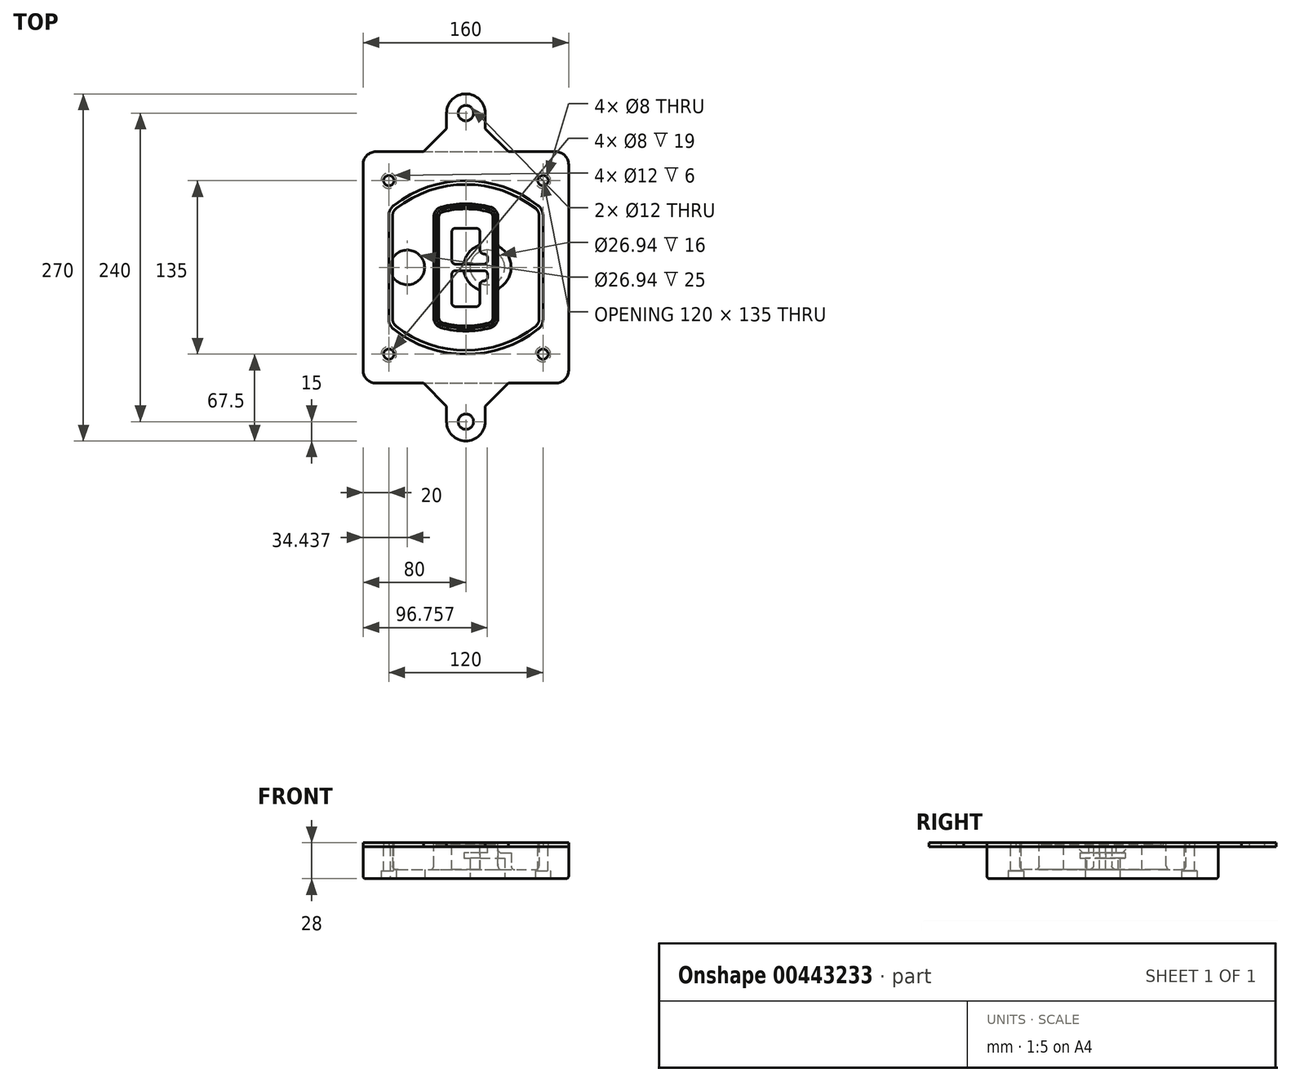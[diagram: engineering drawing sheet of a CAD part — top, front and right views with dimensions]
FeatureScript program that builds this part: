
annotation { "Feature Type Name" : "Feature", "Feature Type Description" : "" }
export const myFeature = defineFeature(function(context is Context, id is Id, definition is map)
    precondition{}
    {
        {
            var Q0;
            Q0=qCreatedBy(makeId("Top.planeOp"),FACE);
            var sketch = newSketch(context, id + "F0", { "sketchPlane" : qUnion([Q0])});
            skPoint(sketch, "E0.rect.middle", {"position": v(0, 0) * mm});
            skLineSegment(sketch, "E1.bottom", {"start": v(-70, -90) * mm, "end": v(70, -90) * mm});
            skLineSegment(sketch, "E1.top", {"start": v(-70, 90) * mm, "end": v(70, 90) * mm});
            skLineSegment(sketch, "E1.left", {"start": v(-80, -80) * mm, "end": v(-80, 80) * mm});
            skLineSegment(sketch, "E1.right", {"start": v(80, -80) * mm, "end": v(80, 80) * mm});
            skLineSegment(sketch, "E2", {"start": v(-80, 90) * mm, "end": v(80, -90) * mm, "construction": true});
            skLineSegment(sketch, "E3", {"start": v(80, 90) * mm, "end": v(-80, -90) * mm, "construction": true});
            skCircle(sketch, "E4", {"center": v(-60, 67.5) * mm, "radius": 4 * mm});
            skCircle(sketch, "E5", {"center": v(60, 67.5) * mm, "radius": 4 * mm});
            skCircle(sketch, "E6", {"center": v(60, -67.5) * mm, "radius": 4 * mm});
            skCircle(sketch, "E7", {"center": v(-60, -67.5) * mm, "radius": 4 * mm});
            skLineSegment(sketch, "E8", {"start": v(-60, 67.5) * mm, "end": v(60, 67.5) * mm, "construction": true});
            skLineSegment(sketch, "E9", {"start": v(60, 67.5) * mm, "end": v(60, -67.5) * mm, "construction": true});
            skLineSegment(sketch, "E10", {"start": v(60, -67.5) * mm, "end": v(-60, -67.5) * mm, "construction": true});
            skLineSegment(sketch, "E11", {"start": v(-60, -67.5) * mm, "end": v(-60, 67.5) * mm, "construction": true});
            skLineSegment(sketch, "E12", {"start": v(-60, 40.3) * mm, "end": v(-60, -40.3) * mm});
            skLineSegment(sketch, "E13", {"start": v(60, 40.3) * mm, "end": v(60, -40.3) * mm});
            skArc(sketch, "E14", {"start": v(56.15, 48.18) * mm, "mid": v(0, 67.5) * mm, "end": v(-56.15, 48.18) * mm});
            skArc(sketch, "E15", {"start": v(-56.15, -48.18) * mm, "mid": v(0, -67.5) * mm, "end": v(56.15, -48.18) * mm});
            skLineSegment(sketch, "E16", {"start": v(-60, 0) * mm, "end": v(60, 0) * mm, "construction": true});
            skPoint(sketch, "E17.visualSharp", {"position": v(-60, -45) * mm});
            skArc(sketch, "E17.filletArc", {"start": v(-60, -40.3) * mm, "mid": v(-58.99, -44.68) * mm, "end": v(-56.15, -48.18) * mm});
            skPoint(sketch, "E18.visualSharp", {"position": v(-60, 45) * mm});
            skArc(sketch, "E18.filletArc", {"start": v(-56.15, 48.18) * mm, "mid": v(-58.99, 44.68) * mm, "end": v(-60, 40.3) * mm});
            skPoint(sketch, "E19.visualSharp", {"position": v(60, 45) * mm});
            skArc(sketch, "E19.filletArc", {"start": v(60, 40.3) * mm, "mid": v(58.99, 44.68) * mm, "end": v(56.15, 48.18) * mm});
            skPoint(sketch, "E20.visualSharp", {"position": v(60, -45) * mm});
            skArc(sketch, "E20.filletArc", {"start": v(56.15, -48.18) * mm, "mid": v(58.99, -44.68) * mm, "end": v(60, -40.3) * mm});
            skPoint(sketch, "E21.visualSharp", {"position": v(-80, 90) * mm});
            skArc(sketch, "E21.filletArc", {"start": v(-70, 90) * mm, "mid": v(-77.07, 87.07) * mm, "end": v(-80, 80) * mm});
            skPoint(sketch, "E22.visualSharp", {"position": v(80, 90) * mm});
            skArc(sketch, "E22.filletArc", {"start": v(80, 80) * mm, "mid": v(77.07, 87.07) * mm, "end": v(70, 90) * mm});
            skPoint(sketch, "E23.visualSharp", {"position": v(80, -90) * mm});
            skArc(sketch, "E23.filletArc", {"start": v(70, -90) * mm, "mid": v(77.07, -87.07) * mm, "end": v(80, -80) * mm});
            skPoint(sketch, "E24.visualSharp", {"position": v(-80, -90) * mm});
            skArc(sketch, "E24.filletArc", {"start": v(-80, -80) * mm, "mid": v(-77.07, -87.07) * mm, "end": v(-70, -90) * mm});
            skArc(sketch, "E25.0", {"start": v(57, 40.3) * mm, "mid": v(56.3, 43.36) * mm, "end": v(54.3, 45.81) * mm});
            skLineSegment(sketch, "E25.1", {"start": v(57, 40.3) * mm, "end": v(57, -40.3) * mm});
            skArc(sketch, "E25.2", {"start": v(54.3, -45.81) * mm, "mid": v(56.3, -43.36) * mm, "end": v(57, -40.3) * mm});
            skArc(sketch, "E25.3", {"start": v(-54.3, -45.81) * mm, "mid": v(0, -64.5) * mm, "end": v(54.3, -45.81) * mm});
            skArc(sketch, "E25.4", {"start": v(-57, -40.3) * mm, "mid": v(-56.3, -43.36) * mm, "end": v(-54.3, -45.81) * mm});
            skArc(sketch, "E25.5", {"start": v(54.3, 45.81) * mm, "mid": v(0, 64.5) * mm, "end": v(-54.3, 45.81) * mm});
            skLineSegment(sketch, "E25.6", {"start": v(-57, 40.3) * mm, "end": v(-57, -40.3) * mm});
            skArc(sketch, "E25.7", {"start": v(-54.3, 45.81) * mm, "mid": v(-56.3, 43.36) * mm, "end": v(-57, 40.3) * mm});
            skArc(sketch, "E26.0", {"start": v(-58.62, 51.33) * mm, "mid": v(-62.58, 46.43) * mm, "end": v(-64, 40.3) * mm});
            skArc(sketch, "E26.1", {"start": v(58.62, 51.33) * mm, "mid": v(0, 71.5) * mm, "end": v(-58.62, 51.33) * mm});
            skArc(sketch, "E26.2", {"start": v(64, 40.3) * mm, "mid": v(62.58, 46.43) * mm, "end": v(58.62, 51.33) * mm});
            skLineSegment(sketch, "E26.3", {"start": v(64, 40.3) * mm, "end": v(64, -40.3) * mm});
            skArc(sketch, "E26.4", {"start": v(58.62, -51.33) * mm, "mid": v(62.58, -46.43) * mm, "end": v(64, -40.3) * mm});
            skLineSegment(sketch, "E26.5", {"start": v(-64, 40.3) * mm, "end": v(-64, -40.3) * mm});
            skArc(sketch, "E26.6", {"start": v(-58.62, -51.33) * mm, "mid": v(0, -71.5) * mm, "end": v(58.62, -51.33) * mm});
            skArc(sketch, "E26.7", {"start": v(-64, -40.3) * mm, "mid": v(-62.58, -46.43) * mm, "end": v(-58.62, -51.33) * mm});
            skSolve(sketch);
        }
        {
            var Q0;
            Q0=makeQuery(id+"F0.imprint","IMPRINT",FACE,{"disambiguationData":[TD([[makeQuery(id+"F0.imprint","IMPRINT",EDGE,{"derivedFrom":sQuery(id+"F0.wireOp",EDGE,"E1.bottom")}),1.0]])]});
            var Q1;
            Q1=makeQuery(id+"F0.imprint","IMPRINT",FACE,{"disambiguationData":[TD([[makeQuery(id+"F0.imprint","IMPRINT",EDGE,{"derivedFrom":sQuery(id+"F0.wireOp",EDGE,"E12")}),1.0]])]});
            var Q2;
            Q2=makeQuery(id+"F0.imprint","IMPRINT",FACE,{"disambiguationData":[TD([[makeQuery(id+"F0.imprint","IMPRINT",EDGE,{"derivedFrom":sQuery(id+"F0.wireOp",EDGE,"E25.0")}),1.0]])]});
            var Q3;
            Q3=makeQuery(id+"F0.imprint","IMPRINT",FACE,{"disambiguationData":[TD([[makeQuery(id+"F0.imprint","IMPRINT",EDGE,{"derivedFrom":sQuery(id+"F0.wireOp",EDGE,"E12")}),-1.0]])]});
            extrude(context, id + "F1", {"entities" : qUnion([Q0, Q1, Q2, Q3]), "oppositeDirection" : true, "depth" : 25 * mm});
        }
        {
            var Q0;
            Q0=makeQuery(id+"F0.imprint","IMPRINT",FACE,{"disambiguationData":[TD([[makeQuery(id+"F0.imprint","IMPRINT",EDGE,{"derivedFrom":sQuery(id+"F0.wireOp",EDGE,"E12")}),1.0]])]});
            extrude(context, id + "F2", {"entities" : qUnion([Q0]), "operationType" : NewBodyOperationType.ADD, "depth" : 3 * mm});
        }
        {
            var Q0;
            Q0=makeQuery(id+"F0.imprint","IMPRINT",FACE,{"disambiguationData":[TD([[makeQuery(id+"F0.imprint","IMPRINT",EDGE,{"derivedFrom":sQuery(id+"F0.wireOp",EDGE,"E25.0")}),1.0]])]});
            extrude(context, id + "F3", {"entities" : qUnion([Q0]), "operationType" : NewBodyOperationType.REMOVE, "oppositeDirection" : true, "depth" : 18 * mm});
        }
        {
            var Q0;
            Q0=makeQuery(id+"F2.opExtrude","CAP_FACE",FACE,{"disambiguationData":[OSD([sQuery(id+"F0.wireOp",EDGE,"E12"),sQuery(id+"F0.wireOp",EDGE,"E13"),sQuery(id+"F0.wireOp",EDGE,"E14"),sQuery(id+"F0.wireOp",EDGE,"E15"),sQuery(id+"F0.wireOp",EDGE,"E17.filletArc"),sQuery(id+"F0.wireOp",EDGE,"E18.filletArc"),sQuery(id+"F0.wireOp",EDGE,"E19.filletArc"),sQuery(id+"F0.wireOp",EDGE,"E20.filletArc"),sQuery(id+"F0.wireOp",EDGE,"E25.0"),sQuery(id+"F0.wireOp",EDGE,"E25.1"),sQuery(id+"F0.wireOp",EDGE,"E25.2"),sQuery(id+"F0.wireOp",EDGE,"E25.3"),sQuery(id+"F0.wireOp",EDGE,"E25.4"),sQuery(id+"F0.wireOp",EDGE,"E25.5"),sQuery(id+"F0.wireOp",EDGE,"E25.6"),sQuery(id+"F0.wireOp",EDGE,"E25.7")])],"isStart":false});
            var sketch = newSketch(context, id + "F4", { "sketchPlane" : qUnion([Q0])});
            skArc(sketch, "E27.0", {"start": v(-19.08, -46.97) * mm, "mid": v(0, -49.5) * mm, "end": v(19.08, -46.97) * mm});
            skArc(sketch, "E28.0", {"start": v(19.08, 46.97) * mm, "mid": v(0, 49.5) * mm, "end": v(-19.08, 46.97) * mm});
            skLineSegment(sketch, "E29", {"start": v(-25, 39.25) * mm, "end": v(-25, -39.25) * mm});
            skLineSegment(sketch, "E30", {"start": v(25, 39.25) * mm, "end": v(25, -39.25) * mm});
            skLineSegment(sketch, "E31", {"start": v(-25, 45.1) * mm, "end": v(25, 45.1) * mm, "construction": true});
            skLineSegment(sketch, "E32", {"start": v(-25, -45.1) * mm, "end": v(25, -45.1) * mm, "construction": true});
            skPoint(sketch, "E33.visualSharp", {"position": v(-25, 45.1) * mm});
            skArc(sketch, "E33.filletArc", {"start": v(-19.08, 46.97) * mm, "mid": v(-23.35, 44.11) * mm, "end": v(-25, 39.25) * mm});
            skPoint(sketch, "E34.visualSharp", {"position": v(25, 45.1) * mm});
            skArc(sketch, "E34.filletArc", {"start": v(25, 39.25) * mm, "mid": v(23.35, 44.11) * mm, "end": v(19.08, 46.97) * mm});
            skPoint(sketch, "E35.visualSharp", {"position": v(25, -45.1) * mm});
            skArc(sketch, "E35.filletArc", {"start": v(19.08, -46.97) * mm, "mid": v(23.35, -44.11) * mm, "end": v(25, -39.25) * mm});
            skPoint(sketch, "E36.visualSharp", {"position": v(-25, -45.1) * mm});
            skArc(sketch, "E36.filletArc", {"start": v(-25, -39.25) * mm, "mid": v(-23.35, -44.11) * mm, "end": v(-19.08, -46.97) * mm});
            skArc(sketch, "E37.0", {"start": v(54.3, 45.81) * mm, "mid": v(0, 64.5) * mm, "end": v(-54.3, 45.81) * mm});
            skArc(sketch, "E37.1", {"start": v(-54.3, 45.81) * mm, "mid": v(-56.3, 43.36) * mm, "end": v(-57, 40.3) * mm});
            skLineSegment(sketch, "E37.2", {"start": v(-57, 40.3) * mm, "end": v(-57, -40.3) * mm});
            skArc(sketch, "E37.3", {"start": v(-57, -40.3) * mm, "mid": v(-56.3, -43.36) * mm, "end": v(-54.3, -45.81) * mm});
            skArc(sketch, "E37.4", {"start": v(-54.3, -45.81) * mm, "mid": v(0, -64.5) * mm, "end": v(54.3, -45.81) * mm});
            skArc(sketch, "E37.5", {"start": v(54.3, -45.81) * mm, "mid": v(56.3, -43.36) * mm, "end": v(57, -40.3) * mm});
            skLineSegment(sketch, "E37.6", {"start": v(57, 40.3) * mm, "end": v(57, -40.3) * mm});
            skArc(sketch, "E37.7", {"start": v(57, 40.3) * mm, "mid": v(56.3, 43.36) * mm, "end": v(54.3, 45.81) * mm});
            skLineSegment(sketch, "E38.0", {"start": v(23, 39.25) * mm, "end": v(23, -39.25) * mm});
            skArc(sketch, "E38.1", {"start": v(18.56, -45.04) * mm, "mid": v(21.76, -42.9) * mm, "end": v(23, -39.25) * mm});
            skArc(sketch, "E38.2", {"start": v(-18.56, -45.04) * mm, "mid": v(0, -47.5) * mm, "end": v(18.56, -45.04) * mm});
            skArc(sketch, "E38.3", {"start": v(-23, -39.25) * mm, "mid": v(-21.76, -42.9) * mm, "end": v(-18.56, -45.04) * mm});
            skLineSegment(sketch, "E38.4", {"start": v(-23, 39.25) * mm, "end": v(-23, -39.25) * mm});
            skArc(sketch, "E38.5", {"start": v(23, 39.25) * mm, "mid": v(21.76, 42.9) * mm, "end": v(18.56, 45.04) * mm});
            skArc(sketch, "E38.6", {"start": v(-18.56, 45.04) * mm, "mid": v(-21.76, 42.9) * mm, "end": v(-23, 39.25) * mm});
            skArc(sketch, "E38.7", {"start": v(18.56, 45.04) * mm, "mid": v(0, 47.5) * mm, "end": v(-18.56, 45.04) * mm});
            skArc(sketch, "E39.0", {"start": v(21, 39.25) * mm, "mid": v(20.18, 41.68) * mm, "end": v(18.04, 43.1) * mm});
            skLineSegment(sketch, "E39.1", {"start": v(21, 39.25) * mm, "end": v(21, -39.25) * mm});
            skArc(sketch, "E39.2", {"start": v(18.04, -43.1) * mm, "mid": v(20.18, -41.68) * mm, "end": v(21, -39.25) * mm});
            skArc(sketch, "E39.3", {"start": v(-18.04, -43.1) * mm, "mid": v(0, -45.5) * mm, "end": v(18.04, -43.1) * mm});
            skArc(sketch, "E39.4", {"start": v(-21, -39.25) * mm, "mid": v(-20.18, -41.68) * mm, "end": v(-18.04, -43.1) * mm});
            skArc(sketch, "E39.5", {"start": v(18.04, 43.1) * mm, "mid": v(0, 45.5) * mm, "end": v(-18.04, 43.1) * mm});
            skLineSegment(sketch, "E39.6", {"start": v(-21, 39.25) * mm, "end": v(-21, -39.25) * mm});
            skArc(sketch, "E39.7", {"start": v(-18.04, 43.1) * mm, "mid": v(-20.18, 41.68) * mm, "end": v(-21, 39.25) * mm});
            skLineSegment(sketch, "E40", {"start": v(-25, 0) * mm, "end": v(25, 0) * mm, "construction": true});
            skLineSegment(sketch, "E41", {"start": v(-11, 5.5) * mm, "end": v(-11, 27.5) * mm});
            skLineSegment(sketch, "E42", {"start": v(-8, 30.5) * mm, "end": v(8, 30.5) * mm});
            skLineSegment(sketch, "E43", {"start": v(11, 27.5) * mm, "end": v(11, 13.5) * mm});
            skLineSegment(sketch, "E44", {"start": v(14, 10.5) * mm, "end": v(14, 10.5) * mm});
            skLineSegment(sketch, "E45", {"start": v(17, 7.5) * mm, "end": v(17, 5.5) * mm});
            skLineSegment(sketch, "E46", {"start": v(14, 2.5) * mm, "end": v(-8, 2.5) * mm});
            skPoint(sketch, "E47.visualSharp", {"position": v(-11, 30.5) * mm});
            skArc(sketch, "E47.filletArc", {"start": v(-8, 30.5) * mm, "mid": v(-10.12, 29.62) * mm, "end": v(-11, 27.5) * mm});
            skPoint(sketch, "E48.visualSharp", {"position": v(11, 30.5) * mm});
            skArc(sketch, "E48.filletArc", {"start": v(11, 27.5) * mm, "mid": v(10.12, 29.62) * mm, "end": v(8, 30.5) * mm});
            skPoint(sketch, "E49.visualSharp", {"position": v(11, 10.5) * mm});
            skArc(sketch, "E49.filletArc", {"start": v(11, 13.5) * mm, "mid": v(11.88, 11.38) * mm, "end": v(14, 10.5) * mm});
            skPoint(sketch, "E50.visualSharp", {"position": v(17, 10.5) * mm});
            skArc(sketch, "E50.filletArc", {"start": v(17, 7.5) * mm, "mid": v(16.12, 9.62) * mm, "end": v(14, 10.5) * mm});
            skPoint(sketch, "E51.visualSharp", {"position": v(17, 2.5) * mm});
            skArc(sketch, "E51.filletArc", {"start": v(14, 2.5) * mm, "mid": v(16.12, 3.38) * mm, "end": v(17, 5.5) * mm});
            skPoint(sketch, "E52.visualSharp", {"position": v(-11, 2.5) * mm});
            skArc(sketch, "E52.filletArc", {"start": v(-11, 5.5) * mm, "mid": v(-10.12, 3.38) * mm, "end": v(-8, 2.5) * mm});
            skLineSegment(sketch, "E53.0.MirrorCS", {"start": v(14, -2.5) * mm, "end": v(-8, -2.5) * mm});
            skArc(sketch, "E54.0.MirrorCS", {"start": v(-11, -5.5) * mm, "mid": v(-10.12, -3.38) * mm, "end": v(-8, -2.5) * mm});
            skLineSegment(sketch, "E55.0.MirrorCS", {"start": v(-11, -5.5) * mm, "end": v(-11, -27.5) * mm});
            skArc(sketch, "E56.0.MirrorCS", {"start": v(-8, -30.5) * mm, "mid": v(-10.12, -29.62) * mm, "end": v(-11, -27.5) * mm});
            skLineSegment(sketch, "E57.0.MirrorCS", {"start": v(-8, -30.5) * mm, "end": v(8, -30.5) * mm});
            skArc(sketch, "E58.0.MirrorCS", {"start": v(11, -27.5) * mm, "mid": v(10.12, -29.62) * mm, "end": v(8, -30.5) * mm});
            skLineSegment(sketch, "E59.0.MirrorCS", {"start": v(11, -27.5) * mm, "end": v(11, -13.5) * mm});
            skArc(sketch, "E60.0.MirrorCS", {"start": v(11, -13.5) * mm, "mid": v(11.88, -11.38) * mm, "end": v(14, -10.5) * mm});
            skArc(sketch, "E61.0.MirrorCS", {"start": v(17, -7.5) * mm, "mid": v(16.12, -9.62) * mm, "end": v(14, -10.5) * mm});
            skLineSegment(sketch, "E62.0.MirrorCS", {"start": v(17, -7.5) * mm, "end": v(17, -5.5) * mm});
            skArc(sketch, "E63.0.MirrorCS", {"start": v(14, -2.5) * mm, "mid": v(16.12, -3.38) * mm, "end": v(17, -5.5) * mm});
            skSolve(sketch);
        }
        {
            var Q0;
            Q0=makeQuery(id+"F4.imprint","IMPRINT",FACE,{"disambiguationData":[TD([[makeQuery(id+"F4.imprint","IMPRINT",EDGE,{"derivedFrom":sQuery(id+"F4.wireOp",EDGE,"E27.0")}),1.0]])]});
            var Q1;
            Q1=makeQuery(id+"F4.imprint","IMPRINT",FACE,{"disambiguationData":[TD([[makeQuery(id+"F4.imprint","IMPRINT",EDGE,{"derivedFrom":sQuery(id+"F4.wireOp",EDGE,"E38.0")}),-1.0]])]});
            var Q2;
            Q2=makeQuery(id+"F4.imprint","IMPRINT",FACE,{"disambiguationData":[TD([[makeQuery(id+"F4.imprint","IMPRINT",EDGE,{"derivedFrom":sQuery(id+"F4.wireOp",EDGE,"E39.0")}),1.0]])]});
            extrude(context, id + "F5", {"entities" : qUnion([Q0, Q1, Q2]), "operationType" : NewBodyOperationType.ADD, "endBound" : BoundingType.UP_TO_NEXT, "oppositeDirection" : true, "depth" : 25 * mm});
        }
        {
            var Q0;
            Q0=makeQuery(id+"F4.imprint","IMPRINT",FACE,{"disambiguationData":[TD([[makeQuery(id+"F4.imprint","IMPRINT",EDGE,{"derivedFrom":sQuery(id+"F4.wireOp",EDGE,"E38.0")}),-1.0]])]});
            extrude(context, id + "F6", {"entities" : qUnion([Q0]), "operationType" : NewBodyOperationType.REMOVE, "oppositeDirection" : true, "depth" : 2 * mm});
        }
        {
            var Q0;
            Q0=makeQuery(id+"F1.opExtrude","CAP_FACE",FACE,{"disambiguationData":[OSD([sQuery(id+"F0.wireOp",EDGE,"E1.bottom"),sQuery(id+"F0.wireOp",EDGE,"E1.top"),sQuery(id+"F0.wireOp",EDGE,"E1.left"),sQuery(id+"F0.wireOp",EDGE,"E1.right"),sQuery(id+"F0.wireOp",EDGE,"E4"),sQuery(id+"F0.wireOp",EDGE,"E5"),sQuery(id+"F0.wireOp",EDGE,"E6"),sQuery(id+"F0.wireOp",EDGE,"E7"),sQuery(id+"F0.wireOp",EDGE,"E21.filletArc"),sQuery(id+"F0.wireOp",EDGE,"E22.filletArc"),sQuery(id+"F0.wireOp",EDGE,"E23.filletArc"),sQuery(id+"F0.wireOp",EDGE,"E24.filletArc")])],"isStart":false});
            var sketch = newSketch(context, id + "F7", { "sketchPlane" : qUnion([Q0])});
            skCircle(sketch, "E64", {"center": v(16.76, 0) * mm, "radius": 13.47 * mm});
            skCircle(sketch, "E65", {"center": v(-45.56, 0) * mm, "radius": 13.47 * mm});
            skLineSegment(sketch, "E66", {"start": v(80, 0) * mm, "end": v(-80, 0) * mm});
            skCircle(sketch, "E67", {"center": v(16.76, 0) * mm, "radius": 18.47 * mm});
            skCircle(sketch, "E68", {"center": v(60, -67.5) * mm, "radius": 6 * mm});
            skCircle(sketch, "E69", {"center": v(-60, -67.5) * mm, "radius": 6 * mm});
            skCircle(sketch, "E70", {"center": v(-60, 67.5) * mm, "radius": 6 * mm});
            skCircle(sketch, "E71", {"center": v(60, 67.5) * mm, "radius": 6 * mm});
            skSolve(sketch);
        }
        {
            var Q0;
            {var subQ1=sQuery(id+"F7.wireOp",EDGE,"E66");var subQ4=sQuery(id+"F7.wireOp",EDGE,"E64");var subQ6=makeQuery(id+"F7.imprint","INTERSECT",VERTEX,{"disambiguationData":[OD(0.0)],"derivedFrom":[subQ4,subQ1]});Q0=makeQuery(id+"F7.imprint","IMPRINT",FACE,{"disambiguationData":[TD([[makeQuery(id+"F7.imprint","IMPRINT",EDGE,{"disambiguationData":[TD([[subQ6,-1.0]])],"derivedFrom":subQ4}),-1.0]])]});}
            var Q1;
            {var subQ0=sQuery(id+"F7.wireOp",EDGE,"E66");var subQ1=sQuery(id+"F7.wireOp",EDGE,"E64");var subQ3=makeQuery(id+"F7.imprint","INTERSECT",VERTEX,{"disambiguationData":[OD(0.0)],"derivedFrom":[subQ1,subQ0]});Q1=makeQuery(id+"F7.imprint","IMPRINT",FACE,{"disambiguationData":[TD([[makeQuery(id+"F7.imprint","IMPRINT",EDGE,{"disambiguationData":[TD([[subQ3,-1.0]])],"derivedFrom":subQ1}),1.0]])]});}
            var Q2;
            {var subQ0=sQuery(id+"F7.wireOp",EDGE,"E66");var subQ1=sQuery(id+"F7.wireOp",EDGE,"E64");var subQ3=makeQuery(id+"F7.imprint","INTERSECT",VERTEX,{"disambiguationData":[OD(0.0)],"derivedFrom":[subQ1,subQ0]});Q2=makeQuery(id+"F7.imprint","IMPRINT",FACE,{"disambiguationData":[TD([[makeQuery(id+"F7.imprint","IMPRINT",EDGE,{"disambiguationData":[TD([[subQ3,1.0]])],"derivedFrom":subQ1}),1.0]])]});}
            var Q3;
            {var subQ1=sQuery(id+"F7.wireOp",EDGE,"E66");var subQ4=sQuery(id+"F7.wireOp",EDGE,"E64");var subQ6=makeQuery(id+"F7.imprint","INTERSECT",VERTEX,{"disambiguationData":[OD(0.0)],"derivedFrom":[subQ4,subQ1]});Q3=makeQuery(id+"F7.imprint","IMPRINT",FACE,{"disambiguationData":[TD([[makeQuery(id+"F7.imprint","IMPRINT",EDGE,{"disambiguationData":[TD([[subQ6,1.0]])],"derivedFrom":subQ4}),-1.0]])]});}
            extrude(context, id + "F8", {"entities" : qUnion([Q0, Q1, Q2, Q3]), "operationType" : NewBodyOperationType.ADD, "oppositeDirection" : true, "depth" : 20 * mm});
        }
        {
            var Q0;
            {var subQ0=sQuery(id+"F7.wireOp",EDGE,"E66");var subQ1=sQuery(id+"F7.wireOp",EDGE,"E64");var subQ3=makeQuery(id+"F7.imprint","INTERSECT",VERTEX,{"disambiguationData":[OD(0.0)],"derivedFrom":[subQ1,subQ0]});Q0=makeQuery(id+"F7.imprint","IMPRINT",FACE,{"disambiguationData":[TD([[makeQuery(id+"F7.imprint","IMPRINT",EDGE,{"disambiguationData":[TD([[subQ3,-1.0]])],"derivedFrom":subQ1}),1.0]])]});}
            var Q1;
            {var subQ0=sQuery(id+"F7.wireOp",EDGE,"E66");var subQ1=sQuery(id+"F7.wireOp",EDGE,"E64");var subQ3=makeQuery(id+"F7.imprint","INTERSECT",VERTEX,{"disambiguationData":[OD(0.0)],"derivedFrom":[subQ1,subQ0]});Q1=makeQuery(id+"F7.imprint","IMPRINT",FACE,{"disambiguationData":[TD([[makeQuery(id+"F7.imprint","IMPRINT",EDGE,{"disambiguationData":[TD([[subQ3,1.0]])],"derivedFrom":subQ1}),1.0]])]});}
            extrude(context, id + "F9", {"entities" : qUnion([Q0, Q1]), "operationType" : NewBodyOperationType.REMOVE, "oppositeDirection" : true, "depth" : 16 * mm});
        }
        {
            var Q0;
            {var subQ0=sQuery(id+"F7.wireOp",EDGE,"E66");var subQ1=sQuery(id+"F7.wireOp",EDGE,"E65");var subQ3=makeQuery(id+"F7.imprint","INTERSECT",VERTEX,{"disambiguationData":[OD(0.0)],"derivedFrom":[subQ1,subQ0]});Q0=makeQuery(id+"F7.imprint","IMPRINT",FACE,{"disambiguationData":[TD([[makeQuery(id+"F7.imprint","IMPRINT",EDGE,{"disambiguationData":[TD([[subQ3,-1.0]])],"derivedFrom":subQ1}),1.0]])]});}
            var Q1;
            {var subQ0=sQuery(id+"F7.wireOp",EDGE,"E66");var subQ1=sQuery(id+"F7.wireOp",EDGE,"E65");var subQ3=makeQuery(id+"F7.imprint","INTERSECT",VERTEX,{"disambiguationData":[OD(0.0)],"derivedFrom":[subQ1,subQ0]});Q1=makeQuery(id+"F7.imprint","IMPRINT",FACE,{"disambiguationData":[TD([[makeQuery(id+"F7.imprint","IMPRINT",EDGE,{"disambiguationData":[TD([[subQ3,1.0]])],"derivedFrom":subQ1}),1.0]])]});}
            extrude(context, id + "F10", {"entities" : qUnion([Q0, Q1]), "operationType" : NewBodyOperationType.REMOVE, "oppositeDirection" : true, "depth" : 25 * mm});
        }
        {
            var Q0;
            Q0=makeQuery(id+"F7.imprint","IMPRINT",FACE,{"disambiguationData":[TD([[makeQuery(id+"F7.imprint","IMPRINT",EDGE,{"derivedFrom":sQuery(id+"F7.wireOp",EDGE,"E68")}),1.0]])]});
            var Q1;
            Q1=makeQuery(id+"F7.imprint","IMPRINT",FACE,{"disambiguationData":[TD([[makeQuery(id+"F7.imprint","IMPRINT",EDGE,{"derivedFrom":makeQuery(id+"F1.opExtrude","CAP_EDGE",EDGE,{"disambiguationData":[OSD([sQuery(id+"F0.wireOp",EDGE,"E5")])],"isStart":false})}),-1.0]])]});
            var Q2;
            Q2=makeQuery(id+"F7.imprint","IMPRINT",FACE,{"disambiguationData":[TD([[makeQuery(id+"F7.imprint","IMPRINT",EDGE,{"derivedFrom":sQuery(id+"F7.wireOp",EDGE,"E69")}),1.0]])]});
            var Q3;
            Q3=makeQuery(id+"F7.imprint","IMPRINT",FACE,{"disambiguationData":[TD([[makeQuery(id+"F7.imprint","IMPRINT",EDGE,{"derivedFrom":makeQuery(id+"F1.opExtrude","CAP_EDGE",EDGE,{"disambiguationData":[OSD([sQuery(id+"F0.wireOp",EDGE,"E4")])],"isStart":false})}),-1.0]])]});
            var Q4;
            Q4=makeQuery(id+"F7.imprint","IMPRINT",FACE,{"disambiguationData":[TD([[makeQuery(id+"F7.imprint","IMPRINT",EDGE,{"derivedFrom":sQuery(id+"F7.wireOp",EDGE,"E70")}),1.0]])]});
            var Q5;
            Q5=makeQuery(id+"F7.imprint","IMPRINT",FACE,{"disambiguationData":[TD([[makeQuery(id+"F7.imprint","IMPRINT",EDGE,{"derivedFrom":makeQuery(id+"F1.opExtrude","CAP_EDGE",EDGE,{"disambiguationData":[OSD([sQuery(id+"F0.wireOp",EDGE,"E7")])],"isStart":false})}),-1.0]])]});
            var Q6;
            Q6=makeQuery(id+"F7.imprint","IMPRINT",FACE,{"disambiguationData":[TD([[makeQuery(id+"F7.imprint","IMPRINT",EDGE,{"derivedFrom":sQuery(id+"F7.wireOp",EDGE,"E71")}),1.0]])]});
            var Q7;
            Q7=makeQuery(id+"F7.imprint","IMPRINT",FACE,{"disambiguationData":[TD([[makeQuery(id+"F7.imprint","IMPRINT",EDGE,{"derivedFrom":makeQuery(id+"F1.opExtrude","CAP_EDGE",EDGE,{"disambiguationData":[OSD([sQuery(id+"F0.wireOp",EDGE,"E6")])],"isStart":false})}),-1.0]])]});
            extrude(context, id + "F11", {"entities" : qUnion([Q0, Q1, Q2, Q3, Q4, Q5, Q6, Q7]), "operationType" : NewBodyOperationType.REMOVE, "oppositeDirection" : true, "depth" : 6 * mm});
        }
        {
            var Q0;
            Q0=makeQuery(id+"F9.boolean.opBoolean","COPY",FACE,{"derivedFrom":makeQuery(id+"F9.opExtrude","CAP_FACE",FACE,{"disambiguationData":[OSD([sQuery(id+"F7.wireOp",EDGE,"E64")])],"isStart":false})});
            var sketch = newSketch(context, id + "F12", { "sketchPlane" : qUnion([Q0])});
            skArc(sketch, "E72.0", {"start": v(11, 17.55) * mm, "mid": v(2.57, 11.82) * mm, "end": v(-1.54, 2.5) * mm});
            skArc(sketch, "E72.1", {"start": v(-1.54, -2.5) * mm, "mid": v(2.57, -11.82) * mm, "end": v(11, -17.55) * mm});
            skLineSegment(sketch, "E73", {"start": v(-1.54, -2.5) * mm, "end": v(14, -2.5) * mm});
            skLineSegment(sketch, "E74.0", {"start": v(14, 2.5) * mm, "end": v(-1.54, 2.5) * mm});
            skArc(sketch, "E74.1", {"start": v(14, 2.5) * mm, "mid": v(16.12, 3.38) * mm, "end": v(17, 5.5) * mm});
            skLineSegment(sketch, "E74.2", {"start": v(17, 7.5) * mm, "end": v(17, 5.5) * mm});
            skArc(sketch, "E74.3", {"start": v(17, 7.5) * mm, "mid": v(16.12, 9.62) * mm, "end": v(14, 10.5) * mm});
            skArc(sketch, "E74.4", {"start": v(11, 13.5) * mm, "mid": v(11.88, 11.38) * mm, "end": v(14, 10.5) * mm});
            skLineSegment(sketch, "E74.5", {"start": v(11, 17.55) * mm, "end": v(11, 13.5) * mm});
            skLineSegment(sketch, "E74.7", {"start": v(14, -2.5) * mm, "end": v(-1.54, -2.5) * mm});
            skArc(sketch, "E74.8", {"start": v(14, -2.5) * mm, "mid": v(16.12, -3.38) * mm, "end": v(17, -5.5) * mm});
            skLineSegment(sketch, "E74.9", {"start": v(17, -7.5) * mm, "end": v(17, -5.5) * mm});
            skArc(sketch, "E74.10", {"start": v(17, -7.5) * mm, "mid": v(16.12, -9.62) * mm, "end": v(14, -10.5) * mm});
            skArc(sketch, "E74.11", {"start": v(11, -13.5) * mm, "mid": v(11.88, -11.38) * mm, "end": v(14, -10.5) * mm});
            skLineSegment(sketch, "E74.12", {"start": v(11, -17.55) * mm, "end": v(11, -13.5) * mm});
            skPoint(sketch, "E75.orphan", {"position": v(11, -27.5) * mm});
            skPoint(sketch, "E76.orphan", {"position": v(-8, -2.5) * mm});
            skPoint(sketch, "E77.orphan", {"position": v(-8, 2.5) * mm});
            skPoint(sketch, "E78.orphan", {"position": v(11, 27.5) * mm});
            skSolve(sketch);
        }
        {
            var Q0;
            {var subQ7=sQuery(id+"F12.wireOp",EDGE,"E72.0");var subQ14=sQuery(id+"F12.wireOp",EDGE,"E72.1");var subQ16=sQuery(id+"F12.wireOp",EDGE,"E74.1");var subQ18=sQuery(id+"F12.wireOp",EDGE,"E74.8");Q0=qUnion([makeQuery(id+"F12.imprint","IMPRINT",FACE,{"disambiguationData":[TD([[makeQuery(id+"F12.imprint","IMPRINT",EDGE,{"derivedFrom":subQ7}),1.0]])]}),makeQuery(id+"F12.imprint","IMPRINT",FACE,{"disambiguationData":[TD([[makeQuery(id+"F12.imprint","IMPRINT",EDGE,{"derivedFrom":subQ14}),1.0]])]}),makeQuery(id+"F12.imprint","IMPRINT",FACE,{"disambiguationData":[TD([[makeQuery(id+"F12.imprint","IMPRINT",EDGE,{"derivedFrom":subQ16}),1.0]])]}),makeQuery(id+"F12.imprint","IMPRINT",FACE,{"disambiguationData":[TD([[makeQuery(id+"F12.imprint","IMPRINT",EDGE,{"derivedFrom":subQ18}),-1.0]])]})]);}
            var Q1;
            Q1=makeQuery(id+"F5.boolean.opBoolean","SPLIT",FACE,{"disambiguationData":[TD([makeQuery(id+"F5.opExtrude","SWEPT_FACE",FACE,{"disambiguationData":[OSD([sQuery(id+"F4.wireOp",EDGE,"E41")])]})])],"derivedFrom":makeQuery(id+"F3.boolean.opBoolean","COPY",FACE,{"derivedFrom":makeQuery(id+"F3.opExtrude","CAP_FACE",FACE,{"disambiguationData":[OSD([sQuery(id+"F0.wireOp",EDGE,"E25.0"),sQuery(id+"F0.wireOp",EDGE,"E25.1"),sQuery(id+"F0.wireOp",EDGE,"E25.2"),sQuery(id+"F0.wireOp",EDGE,"E25.3"),sQuery(id+"F0.wireOp",EDGE,"E25.4"),sQuery(id+"F0.wireOp",EDGE,"E25.5"),sQuery(id+"F0.wireOp",EDGE,"E25.6"),sQuery(id+"F0.wireOp",EDGE,"E25.7")])],"isStart":false})})});
            extrude(context, id + "F13", {"entities" : qUnion([Q0]), "operationType" : NewBodyOperationType.REMOVE, "endBound" : BoundingType.UP_TO_SURFACE, "endBoundEntityFace" : qUnion([Q1]), "depth" : 25 * mm});
        }
        {
            var Q0;
            Q0=makeQuery(id+"F3.boolean.opBoolean","COPY",EDGE,{"derivedFrom":makeQuery(id+"F3.opExtrude","CAP_EDGE",EDGE,{"disambiguationData":[OSD([sQuery(id+"F0.wireOp",EDGE,"E25.6")])],"isStart":false})});
            var Q1;
            Q1=makeQuery(id+"F8.boolean.opBoolean","INTERSECT",EDGE,{"derivedFrom":[makeQuery(id+"F5.opExtrude","SWEPT_FACE",FACE,{"disambiguationData":[OSD([sQuery(id+"F4.wireOp",EDGE,"E30")])]}),makeQuery(id+"F8.opExtrude","CAP_FACE",FACE,{"disambiguationData":[OSD([sQuery(id+"F7.wireOp",EDGE,"E67")])],"isStart":false})]});
            var Q2;
            Q2=makeQuery(id+"F8.boolean.opBoolean","INTERSECT",EDGE,{"disambiguationData":[OD(1.0)],"derivedFrom":[makeQuery(id+"F5.opExtrude","SWEPT_FACE",FACE,{"disambiguationData":[OSD([sQuery(id+"F4.wireOp",EDGE,"E30")])]}),makeQuery(id+"F8.opExtrude","SWEPT_FACE",FACE,{"disambiguationData":[OSD([sQuery(id+"F7.wireOp",EDGE,"E67")])]})]});
            var Q3;
            {var subQ0=sQuery(id+"F4.wireOp",EDGE,"E30");Q3=makeQuery(id+"F8.boolean.opBoolean","SPLIT",EDGE,{"disambiguationData":[TD([makeQuery(id+"F5.opExtrude","SWEPT_FACE",FACE,{"disambiguationData":[OSD([sQuery(id+"F4.wireOp",EDGE,"E35.filletArc")])]})])],"derivedFrom":makeQuery(id+"F5.opExtrude","CAP_EDGE",EDGE,{"disambiguationData":[OSD([subQ0])],"isStart":false})});}
            var Q4;
            {var subQ0=sQuery(id+"F0.wireOp",EDGE,"E25.7");var subQ1=sQuery(id+"F0.wireOp",EDGE,"E25.1");var subQ2=sQuery(id+"F0.wireOp",EDGE,"E25.6");var subQ3=sQuery(id+"F0.wireOp",EDGE,"E25.5");var subQ4=sQuery(id+"F0.wireOp",EDGE,"E25.4");var subQ5=sQuery(id+"F0.wireOp",EDGE,"E25.0");var subQ6=sQuery(id+"F0.wireOp",EDGE,"E25.2");var subQ7=sQuery(id+"F0.wireOp",EDGE,"E25.3");Q4=makeQuery(id+"F8.boolean.opBoolean","INTERSECT",EDGE,{"derivedFrom":[makeQuery(id+"F5.boolean.opBoolean","SPLIT",FACE,{"disambiguationData":[TD([makeQuery(id+"F2.opExtrude","SWEPT_FACE",FACE,{"disambiguationData":[OSD([subQ5])]})])],"derivedFrom":makeQuery(id+"F3.boolean.opBoolean","COPY",FACE,{"derivedFrom":makeQuery(id+"F3.opExtrude","CAP_FACE",FACE,{"disambiguationData":[OSD([subQ5,subQ1,subQ6,subQ7,subQ4,subQ3,subQ2,subQ0])],"isStart":false})})}),makeQuery(id+"F8.opExtrude","SWEPT_FACE",FACE,{"disambiguationData":[OSD([sQuery(id+"F7.wireOp",EDGE,"E67")])]})]});}
            var Q5;
            Q5=makeQuery(id+"F8.boolean.opBoolean","INTERSECT",EDGE,{"disambiguationData":[OD(0.0)],"derivedFrom":[makeQuery(id+"F5.opExtrude","SWEPT_FACE",FACE,{"disambiguationData":[OSD([sQuery(id+"F4.wireOp",EDGE,"E30")])]}),makeQuery(id+"F8.opExtrude","SWEPT_FACE",FACE,{"disambiguationData":[OSD([sQuery(id+"F7.wireOp",EDGE,"E67")])]})]});
            fillet(context, id + "F14", {"entities" : qUnion([Q0, Q1, Q2, Q3, Q4, Q5]), "radius" : 3 * mm, "tangentPropagation" : true, "allowEdgeOverflow" : false});
        }
        {
            var Q0;
            Q0=makeQuery(id+"F1.opExtrude","CAP_EDGE",EDGE,{"disambiguationData":[OSD([sQuery(id+"F0.wireOp",EDGE,"E1.bottom")])],"isStart":false});
            fillet(context, id + "F15", {"entities" : qUnion([Q0]), "radius" : 2 * mm, "tangentPropagation" : true, "allowEdgeOverflow" : false});
        }
        {
            var Q0;
            {var subQ0=sQuery(id+"F0.wireOp",EDGE,"E21.filletArc");var subQ1=sQuery(id+"F0.wireOp",EDGE,"E7");var subQ2=sQuery(id+"F0.wireOp",EDGE,"E6");var subQ3=sQuery(id+"F0.wireOp",EDGE,"E5");var subQ4=sQuery(id+"F0.wireOp",EDGE,"E4");var subQ5=sQuery(id+"F0.wireOp",EDGE,"E22.filletArc");var subQ6=sQuery(id+"F0.wireOp",EDGE,"E1.bottom");var subQ7=sQuery(id+"F0.wireOp",EDGE,"E1.right");var subQ8=sQuery(id+"F0.wireOp",EDGE,"E1.top");var subQ9=sQuery(id+"F0.wireOp",EDGE,"E1.left");var subQ10=sQuery(id+"F0.wireOp",EDGE,"E23.filletArc");var subQ11=sQuery(id+"F0.wireOp",EDGE,"E24.filletArc");Q0=makeQuery(id+"F2.boolean.opBoolean","SPLIT",FACE,{"disambiguationData":[TD([makeQuery(id+"F1.opExtrude","SWEPT_FACE",FACE,{"disambiguationData":[OSD([subQ6])]})])],"derivedFrom":makeQuery(id+"F1.opExtrude","CAP_FACE",FACE,{"disambiguationData":[OSD([subQ6,subQ8,subQ9,subQ7,subQ4,subQ3,subQ2,subQ1,subQ0,subQ5,subQ10,subQ11])],"isStart":true})});}
            var sketch = newSketch(context, id + "F16", { "sketchPlane" : qUnion([Q0])});
            skLineSegment(sketch, "E79", {"start": v(0, 90) * mm, "end": v(0, 120) * mm, "construction": true});
            skCircle(sketch, "E80", {"center": v(0, 120) * mm, "radius": 6 * mm});
            skArc(sketch, "E81", {"start": v(15, 120) * mm, "mid": v(0, 135) * mm, "end": v(-15, 120) * mm});
            skLineSegment(sketch, "E82", {"start": v(15, 120) * mm, "end": v(15, 108) * mm});
            skLineSegment(sketch, "E83", {"start": v(15, 108) * mm, "end": v(33, 90) * mm});
            skLineSegment(sketch, "E84", {"start": v(-33, 90) * mm, "end": v(-15, 108) * mm});
            skLineSegment(sketch, "E85", {"start": v(-15, 108) * mm, "end": v(-15, 120) * mm});
            skLineSegment(sketch, "E86", {"start": v(-80, 0) * mm, "end": v(80, 0) * mm, "construction": true});
            skLineSegment(sketch, "E87.MirrorCS", {"start": v(15, -108) * mm, "end": v(33, -90) * mm});
            skLineSegment(sketch, "E88.MirrorCS", {"start": v(0, -90) * mm, "end": v(0, -120) * mm, "construction": true});
            skArc(sketch, "E89.MirrorCS", {"start": v(15, -120) * mm, "mid": v(0, -135) * mm, "end": v(-15, -120) * mm});
            skLineSegment(sketch, "E90.MirrorCS", {"start": v(15, -120) * mm, "end": v(15, -108) * mm});
            skLineSegment(sketch, "E91.MirrorCS", {"start": v(-15, -108) * mm, "end": v(-15, -120) * mm});
            skCircle(sketch, "E92.MirrorC", {"center": v(0, -120) * mm, "radius": 6 * mm});
            skLineSegment(sketch, "E93.MirrorCS", {"start": v(-33, -90) * mm, "end": v(-15, -108) * mm});
            skLineSegment(sketch, "E94.MirrorCS", {"start": v(33, -90) * mm, "end": v(-33, -90) * mm});
            skSolve(sketch);
        }
        {
            var Q0;
            Q0=makeQuery(id+"F16.imprint","IMPRINT",FACE,{"disambiguationData":[TD([[makeQuery(id+"F16.imprint","IMPRINT",EDGE,{"derivedFrom":sQuery(id+"F16.wireOp",EDGE,"E80")}),-1.0]])]});
            var Q1;
            Q1=makeQuery(id+"F16.imprint","IMPRINT",FACE,{"disambiguationData":[TD([[makeQuery(id+"F16.imprint","IMPRINT",EDGE,{"derivedFrom":sQuery(id+"F16.wireOp",EDGE,"E87.MirrorCS")}),1.0]])]});
            var Q2;
            {var subQ5=sQuery(id+"F16.wireOp",EDGE,"E94.MirrorCS");Q2=makeQuery(id+"F16.imprint","IMPRINT",FACE,{"disambiguationData":[TD([[makeQuery(id+"F16.imprint","IMPRINT",EDGE,{"derivedFrom":subQ5}),1.0]])]});}
            var Q3;
            Q3=makeQuery(id+"F2.opExtrude","CAP_FACE",FACE,{"disambiguationData":[OSD([sQuery(id+"F0.wireOp",EDGE,"E12"),sQuery(id+"F0.wireOp",EDGE,"E13"),sQuery(id+"F0.wireOp",EDGE,"E14"),sQuery(id+"F0.wireOp",EDGE,"E15"),sQuery(id+"F0.wireOp",EDGE,"E17.filletArc"),sQuery(id+"F0.wireOp",EDGE,"E18.filletArc"),sQuery(id+"F0.wireOp",EDGE,"E19.filletArc"),sQuery(id+"F0.wireOp",EDGE,"E20.filletArc"),sQuery(id+"F0.wireOp",EDGE,"E25.0"),sQuery(id+"F0.wireOp",EDGE,"E25.1"),sQuery(id+"F0.wireOp",EDGE,"E25.2"),sQuery(id+"F0.wireOp",EDGE,"E25.3"),sQuery(id+"F0.wireOp",EDGE,"E25.4"),sQuery(id+"F0.wireOp",EDGE,"E25.5"),sQuery(id+"F0.wireOp",EDGE,"E25.6"),sQuery(id+"F0.wireOp",EDGE,"E25.7")])],"isStart":false});
            extrude(context, id + "F17", {"entities" : qUnion([Q0, Q1, Q2]), "endBound" : BoundingType.UP_TO_SURFACE, "endBoundEntityFace" : qUnion([Q3]), "depth" : 25 * mm});
        }
    });
